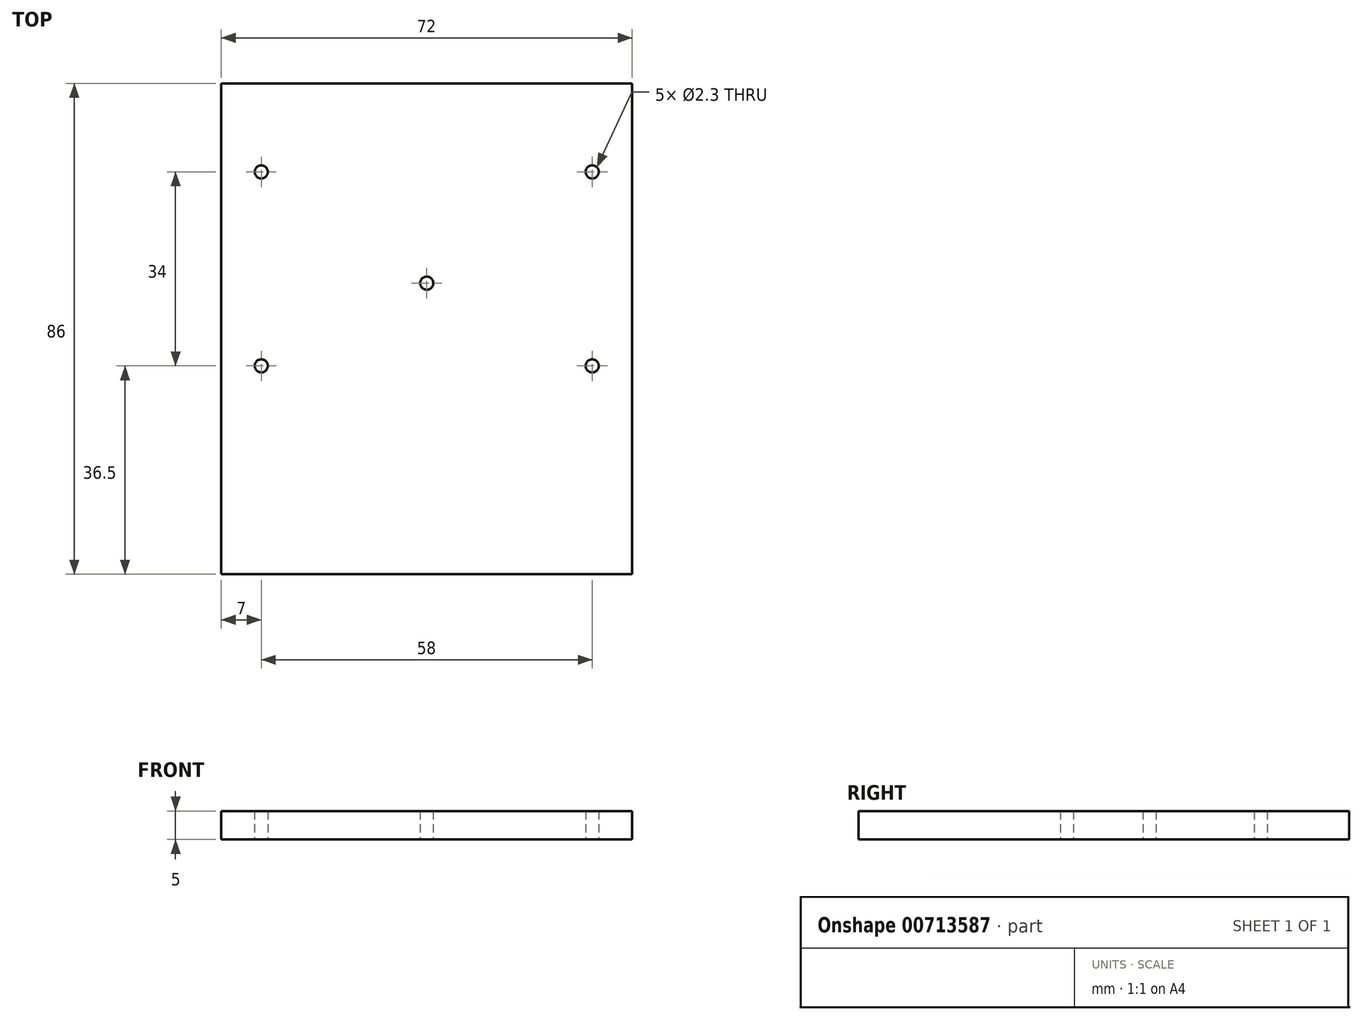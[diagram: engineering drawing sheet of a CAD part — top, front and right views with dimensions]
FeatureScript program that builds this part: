
annotation { "Feature Type Name" : "Feature", "Feature Type Description" : "" }
export const myFeature = defineFeature(function(context is Context, id is Id, definition is map)
    precondition{}
    {
        {
            var Q0;
            Q0=qCreatedBy(makeId("Top.planeOp"),FACE);
            var sketch = newSketch(context, id + "F0", { "sketchPlane" : qUnion([Q0])});
            skLineSegment(sketch, "E0.bottom", {"start": v(-36, 43) * mm, "end": v(36, 43) * mm});
            skLineSegment(sketch, "E0.top", {"start": v(-36, -43) * mm, "end": v(36, -43) * mm});
            skLineSegment(sketch, "E0.left", {"start": v(-36, 43) * mm, "end": v(-36, -43) * mm});
            skLineSegment(sketch, "E0.right", {"start": v(36, 43) * mm, "end": v(36, -43) * mm});
            skPoint(sketch, "E0.middle", {"position": v(0, 0) * mm});
            skLineSegment(sketch, "E1", {"start": v(-36, 27.5) * mm, "end": v(36, 27.5) * mm, "construction": true});
            skLineSegment(sketch, "E2", {"start": v(-36, -6.5) * mm, "end": v(36, -6.5) * mm, "construction": true});
            skLineSegment(sketch, "E3", {"start": v(-29, 43) * mm, "end": v(-29, -43) * mm, "construction": true});
            skLineSegment(sketch, "E4", {"start": v(29, -43) * mm, "end": v(29, 43) * mm, "construction": true});
            skLineSegment(sketch, "E5", {"start": v(-36, 8) * mm, "end": v(36, 8) * mm, "construction": true});
            skLineSegment(sketch, "E6", {"start": v(0, 43) * mm, "end": v(0, -43) * mm, "construction": true});
            skCircle(sketch, "E7", {"center": v(29, 27.5) * mm, "radius": 1.15 * mm});
            skCircle(sketch, "E8", {"center": v(-29, 27.5) * mm, "radius": 1.15 * mm});
            skCircle(sketch, "E9", {"center": v(-29, -6.5) * mm, "radius": 1.15 * mm});
            skCircle(sketch, "E10", {"center": v(29, -6.5) * mm, "radius": 1.15 * mm});
            skCircle(sketch, "E11", {"center": v(0, 8) * mm, "radius": 1.15 * mm});
            skSolve(sketch);
        }
        {
            var Q0;
            Q0=makeQuery(id+"F0.imprint","IMPRINT",FACE,{"disambiguationData":[TD([[makeQuery(id+"F0.imprint","IMPRINT",EDGE,{"derivedFrom":sQuery(id+"F0.wireOp",EDGE,"E0.bottom")}),-1.0]])]});
            extrude(context, id + "F1", {"entities" : qUnion([Q0]), "depth" : 5 * mm, "offsetDistance" : 25 * mm});
        }
    });
